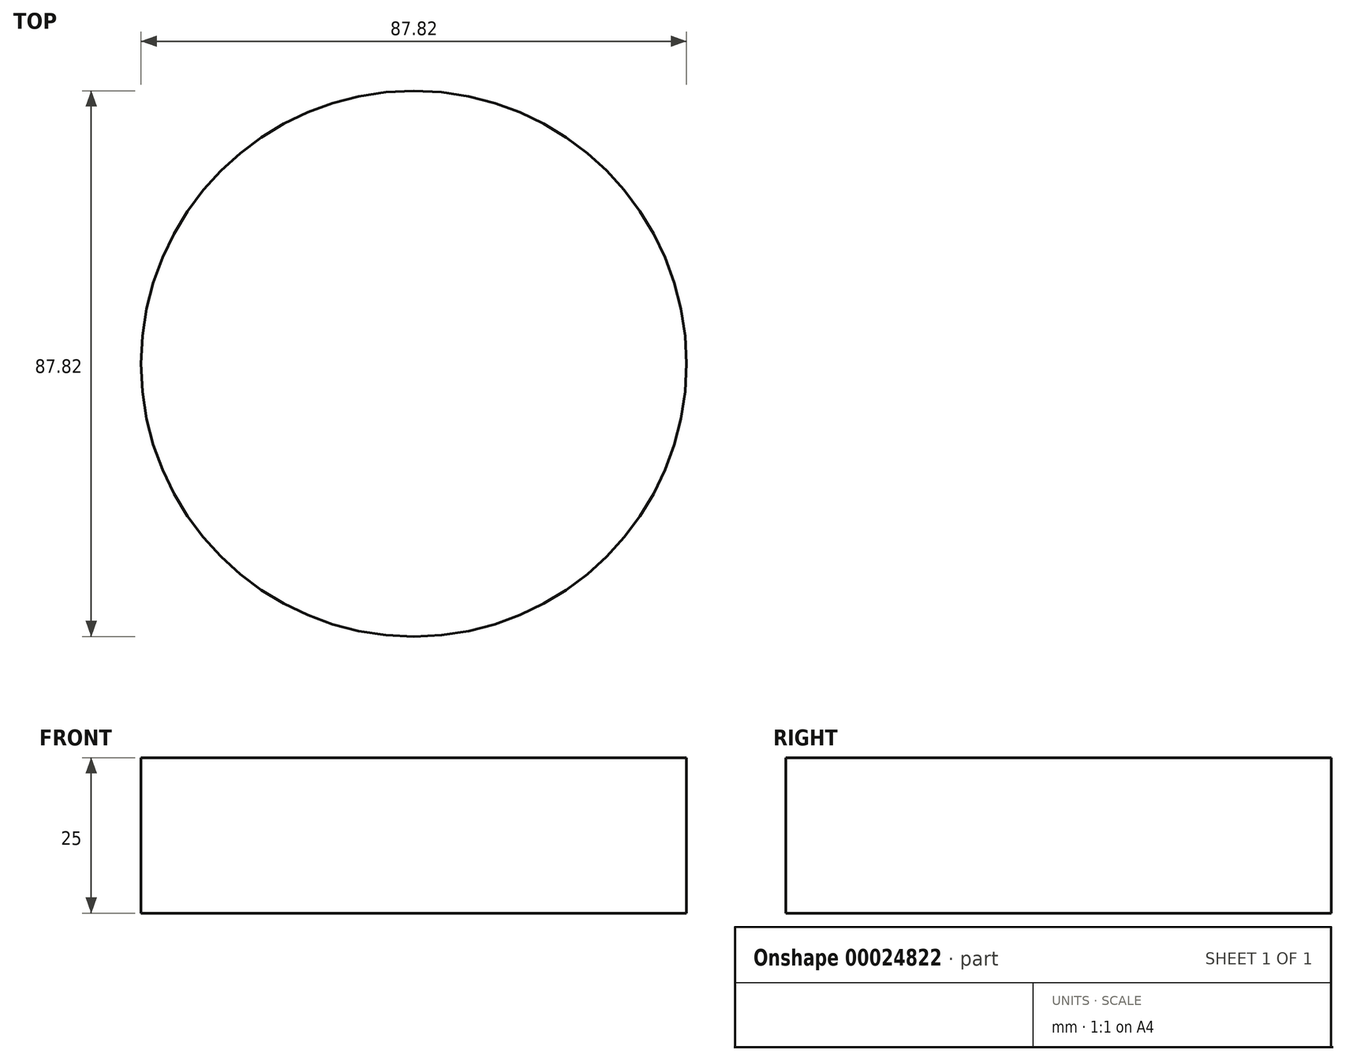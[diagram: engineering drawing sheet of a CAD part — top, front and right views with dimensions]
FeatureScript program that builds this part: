
annotation { "Feature Type Name" : "Feature", "Feature Type Description" : "" }
export const myFeature = defineFeature(function(context is Context, id is Id, definition is map)
    precondition{}
    {
        {
            var Q0;
            Q0=qCreatedBy(makeId("Top.planeOp"),FACE);
            var sketch = newSketch(context, id + "F0", { "sketchPlane" : qUnion([Q0])});
            skCircle(sketch, "E0", {"center": v(0, 0) * mm, "radius": 43.91 * mm});
            skSolve(sketch);
        }
        {
            var Q0;
            Q0 = qSketchRegion(id + "F0", true);
            extrude(context, id + "F1", {"entities" : qUnion([Q0]), "depth" : 25 * mm});
        }
    });
